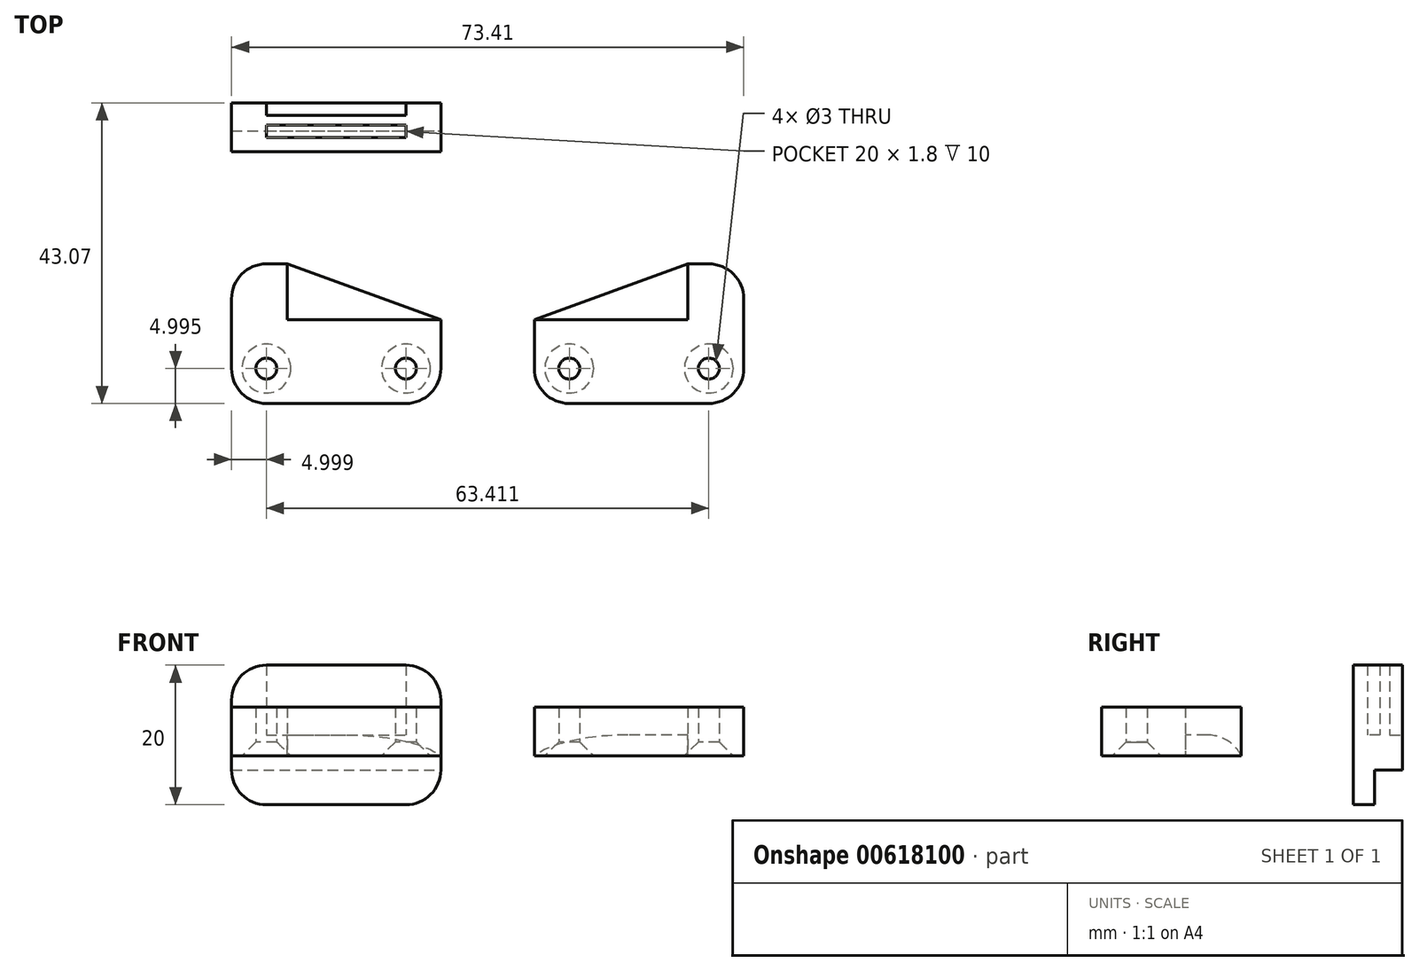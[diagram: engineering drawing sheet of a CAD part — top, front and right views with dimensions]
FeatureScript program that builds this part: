
annotation { "Feature Type Name" : "Feature", "Feature Type Description" : "" }
export const myFeature = defineFeature(function(context is Context, id is Id, definition is map)
    precondition{}
    {
        {
            var Q0;
            Q0=qCreatedBy(makeId("Top.planeOp"),FACE);
            var sketch = newSketch(context, id + "F0", { "sketchPlane" : qUnion([Q0])});
            skLineSegment(sketch, "E0.bottom", {"start": v(2.2, -15.06) * mm, "end": v(5.2, -15.06) * mm});
            skLineSegment(sketch, "E0.top", {"start": v(2.2, -35.06) * mm, "end": v(22.2, -35.06) * mm});
            skLineSegment(sketch, "E0.left", {"start": v(-2.8, -20.06) * mm, "end": v(-2.8, -30.06) * mm});
            skLineSegment(sketch, "E0.right", {"start": v(27.2, -23.06) * mm, "end": v(27.2, -30.06) * mm});
            skLineSegment(sketch, "E1", {"start": v(5.2, -15.06) * mm, "end": v(27.2, -23.06) * mm});
            skLineSegment(sketch, "E2", {"start": v(5.2, -15.06) * mm, "end": v(5.2, -23.06) * mm});
            skLineSegment(sketch, "E3", {"start": v(5.2, -23.06) * mm, "end": v(27.2, -23.06) * mm});
            skPoint(sketch, "E4.visualSharp", {"position": v(-2.8, -15.06) * mm});
            skArc(sketch, "E4.filletArc", {"start": v(2.2, -15.06) * mm, "mid": v(-1.33, -16.53) * mm, "end": v(-2.8, -20.06) * mm});
            skPoint(sketch, "E5.visualSharp", {"position": v(-2.8, -35.06) * mm});
            skArc(sketch, "E5.filletArc", {"start": v(-2.8, -30.06) * mm, "mid": v(-1.33, -33.6) * mm, "end": v(2.2, -35.06) * mm});
            skPoint(sketch, "E6.visualSharp", {"position": v(27.2, -35.06) * mm});
            skArc(sketch, "E6.filletArc", {"start": v(22.2, -35.06) * mm, "mid": v(25.74, -33.6) * mm, "end": v(27.2, -30.06) * mm});
            skLineSegment(sketch, "E7.bottom", {"start": v(62.62, -15.06) * mm, "end": v(65.62, -15.06) * mm});
            skLineSegment(sketch, "E7.top", {"start": v(45.62, -35.06) * mm, "end": v(65.62, -35.06) * mm});
            skLineSegment(sketch, "E7.left", {"start": v(40.62, -23.06) * mm, "end": v(40.62, -30.06) * mm});
            skLineSegment(sketch, "E7.right", {"start": v(70.62, -20.06) * mm, "end": v(70.62, -30.06) * mm});
            skLineSegment(sketch, "E8", {"start": v(62.62, -15.06) * mm, "end": v(62.62, -23.06) * mm});
            skLineSegment(sketch, "E9", {"start": v(62.62, -23.06) * mm, "end": v(40.62, -23.06) * mm});
            skPoint(sketch, "E10.orphan", {"position": v(40.62, -15.06) * mm});
            skLineSegment(sketch, "E11", {"start": v(40.62, -23.06) * mm, "end": v(62.62, -15.06) * mm});
            skPoint(sketch, "E12.visualSharp", {"position": v(70.62, -15.06) * mm});
            skArc(sketch, "E12.filletArc", {"start": v(70.62, -20.06) * mm, "mid": v(69.16, -16.53) * mm, "end": v(65.62, -15.06) * mm});
            skPoint(sketch, "E13.visualSharp", {"position": v(70.62, -35.06) * mm});
            skArc(sketch, "E13.filletArc", {"start": v(65.62, -35.06) * mm, "mid": v(69.16, -33.6) * mm, "end": v(70.62, -30.06) * mm});
            skPoint(sketch, "E14.visualSharp", {"position": v(40.62, -35.06) * mm});
            skArc(sketch, "E14.filletArc", {"start": v(40.62, -30.06) * mm, "mid": v(42.08, -33.6) * mm, "end": v(45.62, -35.06) * mm});
            skCircle(sketch, "E15", {"center": v(2.2, -30.06) * mm, "radius": 1.5 * mm});
            skCircle(sketch, "E16", {"center": v(22.2, -30.06) * mm, "radius": 1.5 * mm});
            skCircle(sketch, "E17", {"center": v(45.62, -30.06) * mm, "radius": 1.5 * mm});
            skCircle(sketch, "E18", {"center": v(65.62, -30.06) * mm, "radius": 1.5 * mm});
            skLineSegment(sketch, "E19.bottom", {"start": v(-2.8, 8) * mm, "end": v(27.2, 8) * mm});
            skLineSegment(sketch, "E19.top", {"start": v(-2.8, 1) * mm, "end": v(27.2, 1) * mm});
            skLineSegment(sketch, "E19.left", {"start": v(-2.8, 8) * mm, "end": v(-2.8, 1) * mm});
            skLineSegment(sketch, "E19.right", {"start": v(27.2, 8) * mm, "end": v(27.2, 1) * mm});
            skLineSegment(sketch, "E20.bottom", {"start": v(2.2, 4.8) * mm, "end": v(22.2, 4.8) * mm});
            skLineSegment(sketch, "E20.top", {"start": v(2.2, 3) * mm, "end": v(22.2, 3) * mm});
            skLineSegment(sketch, "E20.left", {"start": v(2.2, 4.8) * mm, "end": v(2.2, 3) * mm});
            skLineSegment(sketch, "E20.right", {"start": v(22.2, 4.8) * mm, "end": v(22.2, 3) * mm});
            skLineSegment(sketch, "E21", {"start": v(-2.8, 4) * mm, "end": v(27.2, 4) * mm});
            skLineSegment(sketch, "E22", {"start": v(2.2, 8) * mm, "end": v(2.2, 6.2) * mm});
            skLineSegment(sketch, "E23", {"start": v(2.2, 6.2) * mm, "end": v(22.2, 6.2) * mm});
            skLineSegment(sketch, "E24", {"start": v(22.2, 6.2) * mm, "end": v(22.2, 8) * mm});
            skSolve(sketch);
        }
        {
            var Q0;
            Q0=makeQuery(id+"F0.imprint","IMPRINT",FACE,{"disambiguationData":[TD([[makeQuery(id+"F0.imprint","IMPRINT",EDGE,{"derivedFrom":sQuery(id+"F0.wireOp",EDGE,"E0.top")}),1.0]])]});
            var Q1;
            Q1=makeQuery(id+"F0.imprint","IMPRINT",FACE,{"disambiguationData":[TD([[makeQuery(id+"F0.imprint","IMPRINT",EDGE,{"derivedFrom":sQuery(id+"F0.wireOp",EDGE,"E7.bottom")}),-1.0]])]});
            extrude(context, id + "F1", {"entities" : qUnion([Q0, Q1]), "depth" : 4 * mm, "offsetDistance" : 25 * mm});
        }
        {
            var Q0;
            {var subQ0=sQuery(id+"F0.wireOp",EDGE,"E1");Q0=makeQuery(id+"F0.imprint","IMPRINT",FACE,{"disambiguationData":[TD([[makeQuery(id+"F0.imprint","IMPRINT",EDGE,{"derivedFrom":subQ0}),-1.0]])]});}
            var Q1;
            Q1=makeQuery(id+"F0.imprint","IMPRINT",FACE,{"disambiguationData":[TD([[makeQuery(id+"F0.imprint","IMPRINT",EDGE,{"derivedFrom":sQuery(id+"F0.wireOp",EDGE,"E0.top")}),1.0]])]});
            var Q2;
            Q2=makeQuery(id+"F0.imprint","IMPRINT",FACE,{"disambiguationData":[TD([[makeQuery(id+"F0.imprint","IMPRINT",EDGE,{"derivedFrom":sQuery(id+"F0.wireOp",EDGE,"E7.bottom")}),-1.0]])]});
            var Q3;
            Q3=makeQuery(id+"F0.imprint","IMPRINT",FACE,{"disambiguationData":[TD([[makeQuery(id+"F0.imprint","IMPRINT",EDGE,{"derivedFrom":sQuery(id+"F0.wireOp",EDGE,"E8")}),-1.0]])]});
            extrude(context, id + "F2", {"entities" : qUnion([Q0, Q1, Q2, Q3]), "operationType" : NewBodyOperationType.ADD, "oppositeDirection" : true, "depth" : 3 * mm, "offsetDistance" : 25 * mm});
        }
        {
            var Q0;
            Q0=makeQuery(id+"F2.opExtrude","CAP_EDGE",EDGE,{"disambiguationData":[OSD([sQuery(id+"F0.wireOp",EDGE,"E1")])],"isStart":true});
            var Q1;
            Q1=makeQuery(id+"F2.opExtrude","CAP_EDGE",EDGE,{"disambiguationData":[OSD([sQuery(id+"F0.wireOp",EDGE,"E11")])],"isStart":true});
            fillet(context, id + "F3", {"entities" : qUnion([Q0, Q1]), "radius" : 5 * mm, "tangentPropagation" : true, "allowEdgeOverflow" : false});
        }
        {
            var Q0;
            Q0=makeQuery(id+"F2.opExtrude","CAP_EDGE",EDGE,{"disambiguationData":[OSD([sQuery(id+"F0.wireOp",EDGE,"E18")])],"isStart":false});
            var Q1;
            Q1=makeQuery(id+"F2.opExtrude","CAP_EDGE",EDGE,{"disambiguationData":[OSD([sQuery(id+"F0.wireOp",EDGE,"E17")])],"isStart":false});
            var Q2;
            Q2=makeQuery(id+"F2.opExtrude","CAP_EDGE",EDGE,{"disambiguationData":[OSD([sQuery(id+"F0.wireOp",EDGE,"E16")])],"isStart":false});
            var Q3;
            Q3=makeQuery(id+"F2.opExtrude","CAP_EDGE",EDGE,{"disambiguationData":[OSD([sQuery(id+"F0.wireOp",EDGE,"E15")])],"isStart":false});
            chamfer(context, id + "F4", {"entities" : qUnion([Q0, Q1, Q2, Q3]), "width" : 2 * mm, "tangentPropagation" : true});
        }
        {
            var Q0;
            {var subQ3=sQuery(id+"F0.wireOp",EDGE,"E21");Q0=makeQuery(id+"F0.imprint","IMPRINT",FACE,{"disambiguationData":[TD([[makeQuery(id+"F0.imprint","IMPRINT",EDGE,{"derivedFrom":subQ3}),1.0]])]});}
            var Q1;
            {var subQ1=sQuery(id+"F0.wireOp",EDGE,"E19.top");Q1=makeQuery(id+"F0.imprint","IMPRINT",FACE,{"disambiguationData":[TD([[makeQuery(id+"F0.imprint","IMPRINT",EDGE,{"derivedFrom":subQ1}),1.0]])]});}
            extrude(context, id + "F5", {"entities" : qUnion([Q0, Q1]), "depth" : 10 * mm, "offsetDistance" : 25 * mm});
        }
        {
            var Q0;
            {var subQ3=sQuery(id+"F0.wireOp",EDGE,"E21");Q0=makeQuery(id+"F0.imprint","IMPRINT",FACE,{"disambiguationData":[TD([[makeQuery(id+"F0.imprint","IMPRINT",EDGE,{"derivedFrom":subQ3}),1.0]])]});}
            var Q1;
            {var subQ0=sQuery(id+"F0.wireOp",EDGE,"E22");Q1=makeQuery(id+"F0.imprint","IMPRINT",FACE,{"disambiguationData":[TD([[makeQuery(id+"F0.imprint","IMPRINT",EDGE,{"derivedFrom":subQ0}),1.0]])]});}
            var Q2;
            {var subQ1=sQuery(id+"F0.wireOp",EDGE,"E19.top");Q2=makeQuery(id+"F0.imprint","IMPRINT",FACE,{"disambiguationData":[TD([[makeQuery(id+"F0.imprint","IMPRINT",EDGE,{"derivedFrom":subQ1}),1.0]])]});}
            var Q3;
            Q3=makeQuery(id+"F0.imprint","IMPRINT",FACE,{"disambiguationData":[TD([[makeQuery(id+"F0.imprint","IMPRINT",EDGE,{"derivedFrom":sQuery(id+"F0.wireOp",EDGE,"E20.bottom")}),-1.0]])]});
            extrude(context, id + "F6", {"entities" : qUnion([Q0, Q1, Q2, Q3]), "operationType" : NewBodyOperationType.ADD, "oppositeDirection" : true, "depth" : 5 * mm, "offsetDistance" : 25 * mm});
        }
        {
            var Q0;
            {var subQ2=sQuery(id+"F0.wireOp",EDGE,"E19.top");Q0=makeQuery(id+"F0.imprint","IMPRINT",FACE,{"disambiguationData":[TD([[makeQuery(id+"F0.imprint","IMPRINT",EDGE,{"derivedFrom":subQ2}),1.0]])]});}
            var Q1;
            {var subQ0=sQuery(id+"F0.wireOp",EDGE,"E20.top");Q1=makeQuery(id+"F0.imprint","IMPRINT",FACE,{"disambiguationData":[TD([[makeQuery(id+"F0.imprint","IMPRINT",EDGE,{"derivedFrom":subQ0}),1.0]])]});}
            extrude(context, id + "F7", {"entities" : qUnion([Q0, Q1]), "operationType" : NewBodyOperationType.ADD, "oppositeDirection" : true, "depth" : 10 * mm, "offsetDistance" : 25 * mm});
        }
        {
            var Q0;
            Q0=makeQuery(id+"F5.opExtrude","CAP_EDGE",EDGE,{"disambiguationData":[OSD([sQuery(id+"F0.wireOp",EDGE,"E19.left")])],"isStart":false});
            var Q1;
            Q1=makeQuery(id+"F5.opExtrude","CAP_EDGE",EDGE,{"disambiguationData":[OSD([sQuery(id+"F0.wireOp",EDGE,"E19.right")])],"isStart":false});
            var Q2;
            Q2=makeQuery(id+"F7.opExtrude","CAP_EDGE",EDGE,{"disambiguationData":[OSD([sQuery(id+"F0.wireOp",EDGE,"E19.right")])],"isStart":false});
            var Q3;
            Q3=makeQuery(id+"F7.opExtrude","CAP_EDGE",EDGE,{"disambiguationData":[OSD([sQuery(id+"F0.wireOp",EDGE,"E19.left")])],"isStart":false});
            fillet(context, id + "F8", {"entities" : qUnion([Q0, Q1, Q2, Q3]), "radius" : 5 * mm, "tangentPropagation" : true, "allowEdgeOverflow" : false});
        }
    });
